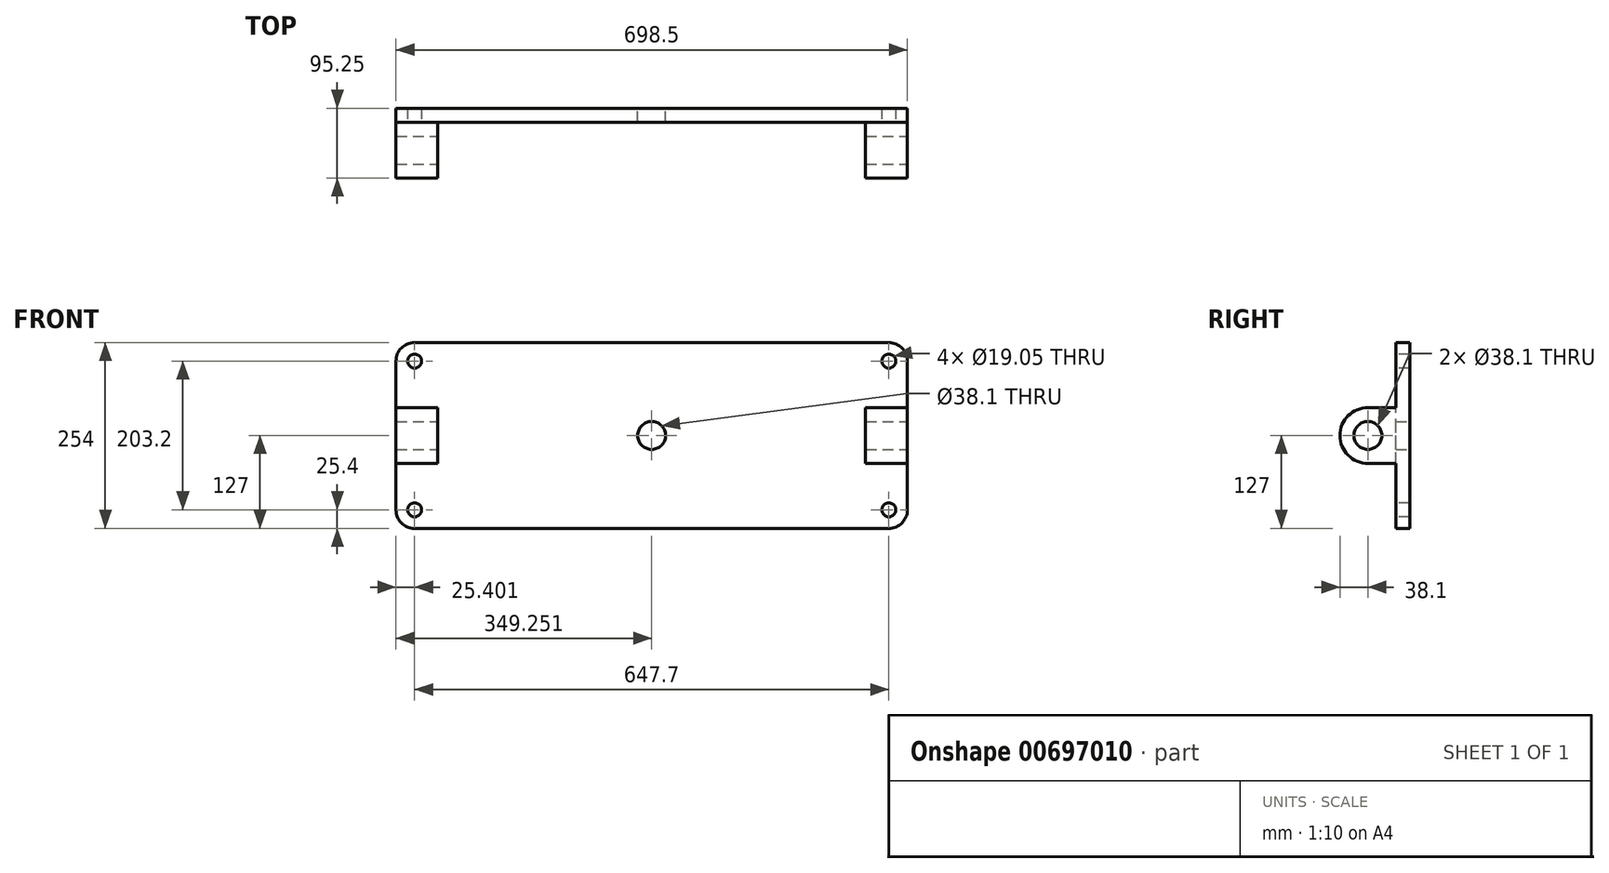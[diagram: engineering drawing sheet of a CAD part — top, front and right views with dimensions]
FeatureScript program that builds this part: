
annotation { "Feature Type Name" : "Feature", "Feature Type Description" : "" }
export const myFeature = defineFeature(function(context is Context, id is Id, definition is map)
    precondition{}
    {
        {
            var Q0;
            Q0=qCreatedBy(makeId("Front.planeOp"),FACE);
            var sketch = newSketch(context, id + "F0", { "sketchPlane" : qUnion([Q0])});
            skLineSegment(sketch, "E0", {"start": v(-304.5, 0) * mm, "end": v(394, 0) * mm});
            skLineSegment(sketch, "E1", {"start": v(-304.5, 0) * mm, "end": v(-304.5, 254) * mm});
            skLineSegment(sketch, "E2", {"start": v(-304.5, 254) * mm, "end": v(394, 254) * mm});
            skLineSegment(sketch, "E3", {"start": v(394, 254) * mm, "end": v(394, 0) * mm});
            skLineSegment(sketch, "E4", {"start": v(44.75, 0) * mm, "end": v(44.75, 127) * mm});
            skCircle(sketch, "E5", {"center": v(44.75, 127) * mm, "radius": 19.05 * mm});
            skSolve(sketch);
        }
        {
            var Q0;
            {var subQ0=sQuery(id+"F0.wireOp",EDGE,"E1");Q0=makeQuery(id+"F0.imprint","IMPRINT",FACE,{"disambiguationData":[TD([[makeQuery(id+"F0.imprint","IMPRINT",EDGE,{"derivedFrom":subQ0}),-1.0]])]});}
            extrude(context, id + "F1", {"entities" : qUnion([Q0]), "depth" : 19.05 * mm});
        }
        {
            var Q0;
            Q0=makeQuery(id+"F1.opExtrude","SWEPT_EDGE",EDGE,{"disambiguationData":[OSD([sQuery(id+"F0.wireOp",EDGE,"E1"),sQuery(id+"F0.wireOp",EDGE,"E2")])]});
            var Q1;
            Q1=makeQuery(id+"F1.opExtrude","SWEPT_EDGE",EDGE,{"disambiguationData":[OSD([sQuery(id+"F0.wireOp",EDGE,"E2"),sQuery(id+"F0.wireOp",EDGE,"E3")])]});
            var Q2;
            Q2=makeQuery(id+"F1.opExtrude","SWEPT_EDGE",EDGE,{"disambiguationData":[OSD([sQuery(id+"F0.wireOp",EDGE,"E0"),sQuery(id+"F0.wireOp",EDGE,"E3")])]});
            var Q3;
            Q3=makeQuery(id+"F1.opExtrude","SWEPT_EDGE",EDGE,{"disambiguationData":[OSD([sQuery(id+"F0.wireOp",EDGE,"E0"),sQuery(id+"F0.wireOp",EDGE,"E1")])]});
            fillet(context, id + "F2", {"entities" : qUnion([Q0, Q1, Q2, Q3]), "radius" : 25.4 * mm, "tangentPropagation" : true, "allowEdgeOverflow" : false});
        }
        {
            var Q0;
            Q0=makeQuery(id+"F1.opExtrude","CAP_FACE",FACE,{"disambiguationData":[OSD([sQuery(id+"F0.wireOp",EDGE,"E0"),sQuery(id+"F0.wireOp",EDGE,"E1"),sQuery(id+"F0.wireOp",EDGE,"E2"),sQuery(id+"F0.wireOp",EDGE,"E3"),sQuery(id+"F0.wireOp",EDGE,"E5")])],"isStart":false});
            var sketch = newSketch(context, id + "F3", { "sketchPlane" : qUnion([Q0])});
            skCircle(sketch, "E6", {"center": v(-279.1, 228.6) * mm, "radius": 9.53 * mm});
            skCircle(sketch, "E7", {"center": v(-279.1, 25.4) * mm, "radius": 9.53 * mm});
            skCircle(sketch, "E8", {"center": v(368.6, 228.6) * mm, "radius": 9.53 * mm});
            skCircle(sketch, "E9", {"center": v(368.6, 25.4) * mm, "radius": 9.53 * mm});
            skSolve(sketch);
        }
        {
            var Q0;
            Q0=makeQuery(id+"F1.opExtrude","CAP_FACE",FACE,{"disambiguationData":[OSD([sQuery(id+"F0.wireOp",EDGE,"E0"),sQuery(id+"F0.wireOp",EDGE,"E1"),sQuery(id+"F0.wireOp",EDGE,"E2"),sQuery(id+"F0.wireOp",EDGE,"E3"),sQuery(id+"F0.wireOp",EDGE,"E5")])],"isStart":false});
            var sketch = newSketch(context, id + "F4", { "sketchPlane" : qUnion([Q0])});
            skLineSegment(sketch, "E10.bottom", {"start": v(-304.5, 127) * mm, "end": v(-247.35, 127) * mm});
            skLineSegment(sketch, "E10.top", {"start": v(-304.5, 88.9) * mm, "end": v(-247.35, 88.9) * mm});
            skLineSegment(sketch, "E10.left", {"start": v(-304.5, 127) * mm, "end": v(-304.5, 88.9) * mm});
            skLineSegment(sketch, "E10.right", {"start": v(-247.35, 127) * mm, "end": v(-247.35, 88.9) * mm});
            skLineSegment(sketch, "E11.top", {"start": v(-304.5, 165.1) * mm, "end": v(-247.35, 165.1) * mm});
            skLineSegment(sketch, "E11.left", {"start": v(-304.5, 127) * mm, "end": v(-304.5, 165.1) * mm});
            skLineSegment(sketch, "E11.right", {"start": v(-247.35, 127) * mm, "end": v(-247.35, 165.1) * mm});
            skLineSegment(sketch, "E12", {"start": v(394, 88.9) * mm, "end": v(394, 165.1) * mm});
            skLineSegment(sketch, "E13", {"start": v(394, 165.1) * mm, "end": v(336.85, 165.1) * mm});
            skLineSegment(sketch, "E14", {"start": v(336.85, 88.9) * mm, "end": v(394, 88.9) * mm});
            skLineSegment(sketch, "E15", {"start": v(336.85, 165.1) * mm, "end": v(336.85, 88.9) * mm});
            skLineSegment(sketch, "E16", {"start": v(336.85, 127) * mm, "end": v(394, 127) * mm});
            skSolve(sketch);
        }
        {
            var Q0;
            Q0=makeQuery(id+"F4.imprint","IMPRINT",FACE,{"disambiguationData":[TD([[makeQuery(id+"F4.imprint","IMPRINT",EDGE,{"derivedFrom":sQuery(id+"F4.wireOp",EDGE,"E10.bottom")}),1.0]])]});
            var Q1;
            Q1=makeQuery(id+"F4.imprint","IMPRINT",FACE,{"disambiguationData":[TD([[makeQuery(id+"F4.imprint","IMPRINT",EDGE,{"derivedFrom":sQuery(id+"F4.wireOp",EDGE,"E10.top")}),1.0]])]});
            extrude(context, id + "F5", {"entities" : qUnion([Q0, Q1]), "operationType" : NewBodyOperationType.ADD, "depth" : 38.1 * mm});
        }
        {
            var Q0;
            Q0=makeQuery(id+"F5.boolean.opBoolean","MERGE",FACE,{"derivedFrom":[makeQuery(id+"F1.opExtrude","SWEPT_FACE",FACE,{"disambiguationData":[OSD([sQuery(id+"F0.wireOp",EDGE,"E1")])]}),makeQuery(id+"F5.opExtrude","SWEPT_FACE",FACE,{"disambiguationData":[OSD([sQuery(id+"F4.wireOp",EDGE,"E10.left"),sQuery(id+"F4.wireOp",EDGE,"E11.left")])]})]});
            var sketch = newSketch(context, id + "F6", { "sketchPlane" : qUnion([Q0])});
            skCircle(sketch, "E17", {"center": v(57.15, 127) * mm, "radius": 38.1 * mm});
            skSolve(sketch);
        }
        {
            var Q0;
            {var subQ1=sQuery(id+"F4.wireOp",EDGE,"E11.left");var subQ2=sQuery(id+"F4.wireOp",EDGE,"E10.left");var subQ3=makeQuery(id+"F5.opExtrude","CAP_EDGE",EDGE,{"disambiguationData":[OSD([subQ2,subQ1])],"isStart":false});Q0=makeQuery(id+"F6.imprint","IMPRINT",FACE,{"disambiguationData":[TD([[makeQuery(id+"F6.imprint","IMPRINT",EDGE,{"derivedFrom":subQ3}),-1.0]])]});}
            extrude(context, id + "F7", {"entities" : qUnion([Q0]), "operationType" : NewBodyOperationType.ADD, "oppositeDirection" : true, "depth" : 57.15 * mm});
        }
        {
            var Q0;
            Q0=makeQuery(id+"F7.boolean.opBoolean","MERGE",FACE,{"derivedFrom":[makeQuery(id+"F5.opExtrude","SWEPT_FACE",FACE,{"disambiguationData":[OSD([sQuery(id+"F4.wireOp",EDGE,"E10.right"),sQuery(id+"F4.wireOp",EDGE,"E11.right")])]}),makeQuery(id+"F7.opExtrude","CAP_FACE",FACE,{"disambiguationData":[OSD([sQuery(id+"F4.wireOp",EDGE,"E10.left"),sQuery(id+"F4.wireOp",EDGE,"E11.left"),sQuery(id+"F6.wireOp",EDGE,"E17")])],"isStart":false})]});
            var sketch = newSketch(context, id + "F8", { "sketchPlane" : qUnion([Q0])});
            skCircle(sketch, "E18", {"center": v(-57.15, 127) * mm, "radius": 19.05 * mm});
            skSolve(sketch);
        }
        {
            var Q0;
            Q0=makeQuery(id+"F1.opExtrude","CAP_FACE",FACE,{"disambiguationData":[OSD([sQuery(id+"F0.wireOp",EDGE,"E0"),sQuery(id+"F0.wireOp",EDGE,"E1"),sQuery(id+"F0.wireOp",EDGE,"E2"),sQuery(id+"F0.wireOp",EDGE,"E3"),sQuery(id+"F0.wireOp",EDGE,"E5")])],"isStart":false});
            var sketch = newSketch(context, id + "F9", { "sketchPlane" : qUnion([Q0])});
            skSolve(sketch);
        }
        {
            var Q0;
            Q0=makeQuery(id+"F8.imprint","IMPRINT",FACE,{"disambiguationData":[TD([[makeQuery(id+"F8.imprint","IMPRINT",EDGE,{"derivedFrom":sQuery(id+"F8.wireOp",EDGE,"E18")}),1.0]])]});
            extrude(context, id + "F10", {"entities" : qUnion([Q0]), "operationType" : NewBodyOperationType.REMOVE, "oppositeDirection" : true, "depth" : 76.2 * mm});
        }
        {
            var Q0;
            Q0=makeQuery(id+"F3.imprint","IMPRINT",FACE,{"disambiguationData":[TD([[makeQuery(id+"F3.imprint","IMPRINT",EDGE,{"derivedFrom":sQuery(id+"F3.wireOp",EDGE,"E6")}),-1.0]])]});
            var sketch = newSketch(context, id + "F11", { "sketchPlane" : qUnion([Q0])});
            skSolve(sketch);
        }
        {
            var Q0;
            Q0=qSketchRegion(id+"F4",true);
            extrude(context, id + "F12", {"entities" : qUnion([Q0]), "operationType" : NewBodyOperationType.ADD, "depth" : 38.1 * mm});
        }
        {
            var Q0;
            Q0=makeQuery(id+"F12.boolean.opBoolean","MERGE",FACE,{"derivedFrom":[makeQuery(id+"F1.opExtrude","SWEPT_FACE",FACE,{"disambiguationData":[OSD([sQuery(id+"F0.wireOp",EDGE,"E3")])]}),makeQuery(id+"F12.opExtrude","SWEPT_FACE",FACE,{"disambiguationData":[OSD([sQuery(id+"F4.wireOp",EDGE,"E12")])]})]});
            var sketch = newSketch(context, id + "F13", { "sketchPlane" : qUnion([Q0])});
            skCircle(sketch, "E19", {"center": v(-57.15, 127) * mm, "radius": 38.1 * mm});
            skSolve(sketch);
        }
        {
            var Q0;
            {var subQ1=sQuery(id+"F4.wireOp",EDGE,"E12");var subQ2=makeQuery(id+"F12.opExtrude","CAP_EDGE",EDGE,{"disambiguationData":[OSD([subQ1])],"isStart":false});Q0=makeQuery(id+"F13.imprint","IMPRINT",FACE,{"disambiguationData":[TD([[makeQuery(id+"F13.imprint","IMPRINT",EDGE,{"derivedFrom":subQ2}),-1.0]])]});}
            extrude(context, id + "F14", {"entities" : qUnion([Q0]), "operationType" : NewBodyOperationType.ADD, "oppositeDirection" : true, "depth" : 57.15 * mm});
        }
        {
            var Q0;
            {var subQ0=sQuery(id+"F4.wireOp",EDGE,"E12");Q0=makeQuery(id+"F14.boolean.opBoolean","MERGE",FACE,{"derivedFrom":[makeQuery(id+"F12.boolean.opBoolean","MERGE",FACE,{"derivedFrom":[makeQuery(id+"F1.opExtrude","SWEPT_FACE",FACE,{"disambiguationData":[OSD([sQuery(id+"F0.wireOp",EDGE,"E3")])]}),makeQuery(id+"F12.opExtrude","SWEPT_FACE",FACE,{"disambiguationData":[OSD([subQ0])]})]}),makeQuery(id+"F14.opExtrude","CAP_FACE",FACE,{"disambiguationData":[OSD([subQ0,sQuery(id+"F13.wireOp",EDGE,"E19")])],"isStart":true})]});}
            var sketch = newSketch(context, id + "F15", { "sketchPlane" : qUnion([Q0])});
            skCircle(sketch, "E20", {"center": v(-57.15, 127) * mm, "radius": 19.05 * mm});
            skSolve(sketch);
        }
        {
            var Q0;
            Q0=makeQuery(id+"F8.imprint","IMPRINT",FACE,{"disambiguationData":[TD([[makeQuery(id+"F8.imprint","IMPRINT",EDGE,{"derivedFrom":sQuery(id+"F8.wireOp",EDGE,"E18")}),1.0]])]});
            extrude(context, id + "F16", {"entities" : qUnion([Q0]), "operationType" : NewBodyOperationType.REMOVE, "oppositeDirection" : true, "depth" : 76.2 * mm});
        }
        {
            var Q0;
            Q0=makeQuery(id+"F15.imprint","IMPRINT",FACE,{"disambiguationData":[TD([[makeQuery(id+"F15.imprint","IMPRINT",EDGE,{"derivedFrom":sQuery(id+"F15.wireOp",EDGE,"E20")}),1.0]])]});
            extrude(context, id + "F17", {"entities" : qUnion([Q0]), "operationType" : NewBodyOperationType.REMOVE, "oppositeDirection" : true, "depth" : 57.15 * mm});
        }
        {
            var Q0;
            Q0=makeQuery(id+"F11.imprint","IMPRINT",FACE,{"disambiguationData":[TD([[makeQuery(id+"F11.imprint","IMPRINT",EDGE,{"derivedFrom":makeQuery(id+"F3.imprint","IMPRINT",EDGE,{"derivedFrom":sQuery(id+"F3.wireOp",EDGE,"E6")})}),1.0]])]});
            var Q1;
            Q1=makeQuery(id+"F11.imprint","IMPRINT",FACE,{"disambiguationData":[TD([[makeQuery(id+"F11.imprint","IMPRINT",EDGE,{"derivedFrom":makeQuery(id+"F3.imprint","IMPRINT",EDGE,{"derivedFrom":sQuery(id+"F3.wireOp",EDGE,"E7")})}),1.0]])]});
            var Q2;
            Q2=makeQuery(id+"F11.imprint","IMPRINT",FACE,{"disambiguationData":[TD([[makeQuery(id+"F11.imprint","IMPRINT",EDGE,{"derivedFrom":makeQuery(id+"F3.imprint","IMPRINT",EDGE,{"derivedFrom":sQuery(id+"F3.wireOp",EDGE,"E8")})}),1.0]])]});
            var Q3;
            Q3=makeQuery(id+"F11.imprint","IMPRINT",FACE,{"disambiguationData":[TD([[makeQuery(id+"F11.imprint","IMPRINT",EDGE,{"derivedFrom":makeQuery(id+"F3.imprint","IMPRINT",EDGE,{"derivedFrom":sQuery(id+"F3.wireOp",EDGE,"E9")})}),1.0]])]});
            extrude(context, id + "F18", {"entities" : qUnion([Q0, Q1, Q2, Q3]), "operationType" : NewBodyOperationType.REMOVE, "oppositeDirection" : true, "depth" : 25.4 * mm});
        }
    });
